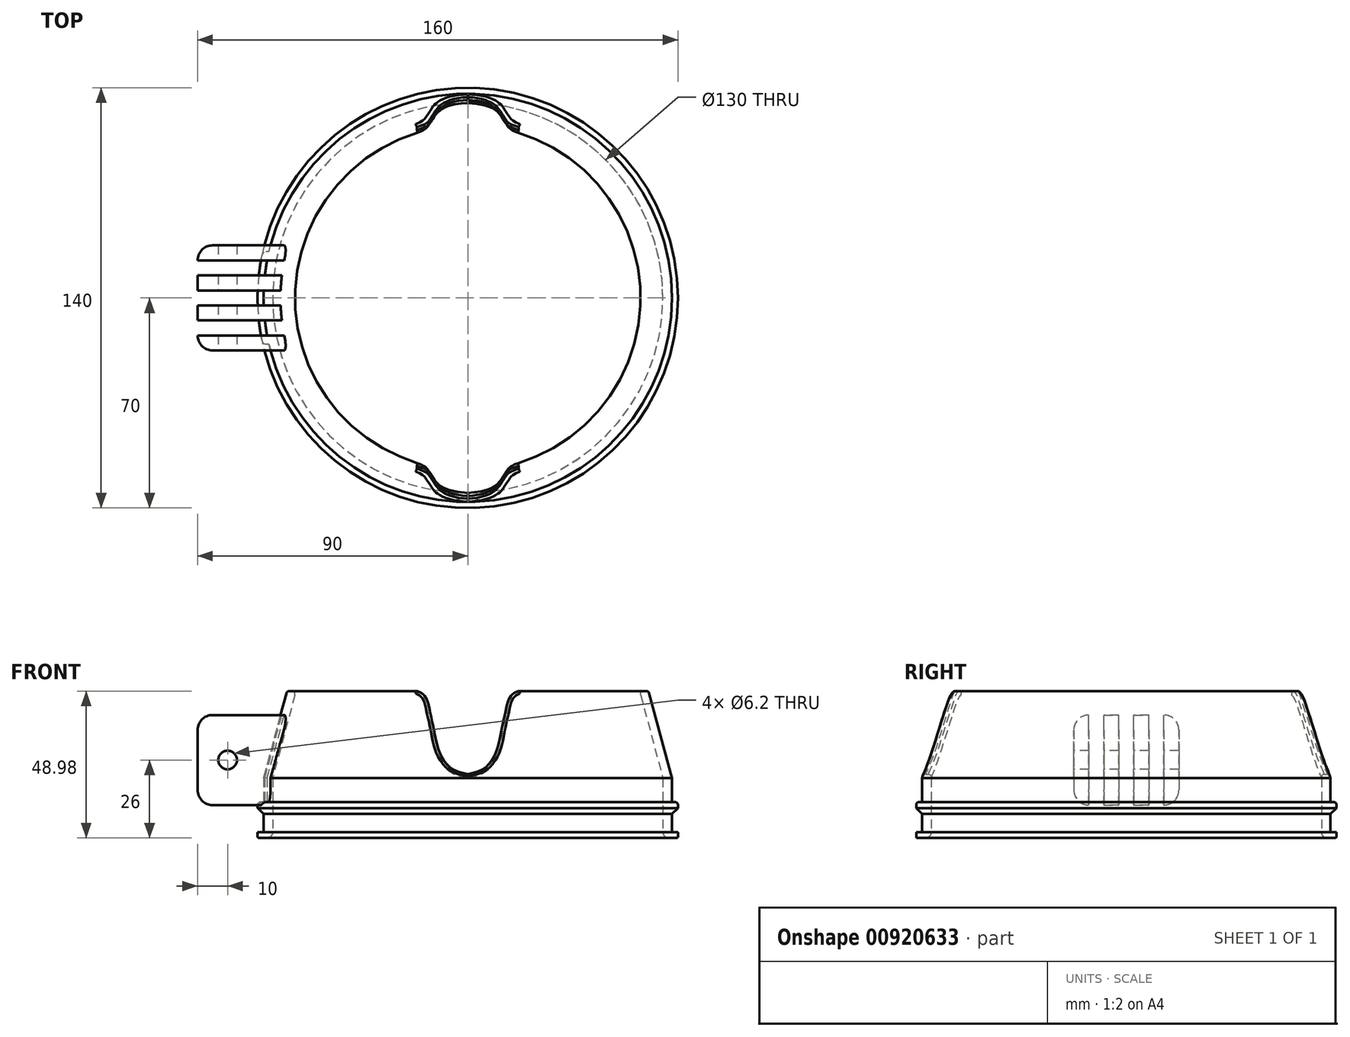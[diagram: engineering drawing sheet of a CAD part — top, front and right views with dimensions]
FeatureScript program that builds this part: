
annotation { "Feature Type Name" : "Feature", "Feature Type Description" : "" }
export const myFeature = defineFeature(function(context is Context, id is Id, definition is map)
    precondition{}
    {
        {
            var Q0;
            Q0=qCreatedBy(makeId("Front.planeOp"),FACE);
            var sketch = newSketch(context, id + "F0", { "sketchPlane" : qUnion([Q0])});
            skLineSegment(sketch, "E0.top", {"start": v(-68, 20) * mm, "end": v(-65, 20) * mm});
            skLineSegment(sketch, "E0.left", {"start": v(-68, 0) * mm, "end": v(-68, 20) * mm});
            skLineSegment(sketch, "E0.right", {"start": v(-65, 0) * mm, "end": v(-65, 20) * mm});
            skLineSegment(sketch, "E1", {"start": v(-68, 20) * mm, "end": v(-60.24, 48.98) * mm});
            skLineSegment(sketch, "E2", {"start": v(-57.24, 48.98) * mm, "end": v(-65, 20) * mm});
            skPoint(sketch, "E3.visualSharp", {"position": v(-68, 0) * mm});
            skPoint(sketch, "E4.visualSharp", {"position": v(-65, 0) * mm});
            skLineSegment(sketch, "E5", {"start": v(-68, 12) * mm, "end": v(-69, 12) * mm});
            skLineSegment(sketch, "E6", {"start": v(-70, 11) * mm, "end": v(-70, 10) * mm});
            skLineSegment(sketch, "E7", {"start": v(-70, 10) * mm, "end": v(-68, 8) * mm});
            skLineSegment(sketch, "E8", {"start": v(-68, 2) * mm, "end": v(-70, 2) * mm});
            skLineSegment(sketch, "E9", {"start": v(-70, 2) * mm, "end": v(-70, 0) * mm});
            skLineSegment(sketch, "E10", {"start": v(-70, 0) * mm, "end": v(-68, 0) * mm});
            skPoint(sketch, "E11.visualSharp", {"position": v(-70, 12) * mm});
            skArc(sketch, "E11.filletArc", {"start": v(-69, 12) * mm, "mid": v(-69.7, 11.7) * mm, "end": v(-70, 11) * mm});
            skLineSegment(sketch, "E12", {"start": v(0, 0) * mm, "end": v(0, 37.2) * mm, "construction": true});
            skLineSegment(sketch, "E13", {"start": v(-60.24, 48.98) * mm, "end": v(-57.24, 48.98) * mm});
            skLineSegment(sketch, "E14", {"start": v(-68, 0) * mm, "end": v(-65, 0) * mm});
            skSolve(sketch);
        }
        {
            var Q0;
            Q0=makeQuery(id+"F0.imprint","IMPRINT",FACE,{"disambiguationData":[TD([[makeQuery(id+"F0.imprint","IMPRINT",EDGE,{"derivedFrom":sQuery(id+"F0.wireOp",EDGE,"E0.bottom")}),1.0]])]});
            var Q1;
            {var subQ0=sQuery(id+"F0.wireOp",EDGE,"E0.top");Q1=makeQuery(id+"F0.imprint","IMPRINT",FACE,{"disambiguationData":[TD([[makeQuery(id+"F0.imprint","IMPRINT",EDGE,{"derivedFrom":subQ0}),1.0]])]});}
            var Q2;
            Q2=makeQuery(id+"F0.imprint","IMPRINT",FACE,{"disambiguationData":[TD([[makeQuery(id+"F0.imprint","IMPRINT",EDGE,{"derivedFrom":sQuery(id+"F0.wireOp",EDGE,"ip61VsO4-G4QX-MuCQ-3TD0-dqhbcXr0CBei")}),1.0]])]});
            var Q3;
            {var subQ1=sQuery(id+"F0.wireOp",EDGE,"E5");Q3=makeQuery(id+"F0.imprint","IMPRINT",FACE,{"disambiguationData":[TD([[makeQuery(id+"F0.imprint","IMPRINT",EDGE,{"derivedFrom":subQ1}),1.0]])]});}
            var Q4;
            {var subQ0=sQuery(id+"F0.wireOp",EDGE,"E8");Q4=makeQuery(id+"F0.imprint","IMPRINT",FACE,{"disambiguationData":[TD([[makeQuery(id+"F0.imprint","IMPRINT",EDGE,{"derivedFrom":subQ0}),1.0]])]});}
            var Q5;
            {var subQ5=sQuery(id+"F0.wireOp",EDGE,"E0.top");Q5=makeQuery(id+"F0.imprint","IMPRINT",FACE,{"disambiguationData":[TD([[makeQuery(id+"F0.imprint","IMPRINT",EDGE,{"derivedFrom":subQ5}),-1.0]])]});}
            var Q6;
            Q6=sQuery(id+"F0.wireOp",EDGE,"E12");
            revolve(context, id + "F1", {"surfaceOperationType" : NewSurfaceOperationType.NEW, "entities" : qUnion([Q0, Q1, Q2, Q3, Q4, Q5]), "axis" : qUnion([Q6]), "revolveType" : RevolveType.FULL});
        }
        {
            var Q0;
            Q0=qCreatedBy(makeId("Front.planeOp"),FACE);
            var sketch = newSketch(context, id + "F2", { "sketchPlane" : qUnion([Q0])});
            skFitSpline(sketch, "E15", {"points": [v(21.47, 49.66) * mm, v(17.18, 49.05) * mm, v(14.22, 47.2) * mm, v(12.69, 42.71) * mm, v(11.26, 35.97) * mm, v(9.52, 28.93) * mm, v(5.64, 23.3) * mm, v(0, 21.26) * mm], "startDerivative": vector(-35.25, -2.77) * mm, "endDerivative": vector(-40.6, -8.65) * mm});
            skFitSpline(sketch, "E16.MirrorCS", {"points": [v(-21.47, 49.66) * mm, v(-17.18, 49.05) * mm, v(-14.22, 47.2) * mm, v(-12.69, 42.71) * mm, v(-11.26, 35.97) * mm, v(-9.52, 28.93) * mm, v(-5.64, 23.3) * mm, v(0, 21.26) * mm], "startDerivative": vector(35.25, -2.77) * mm, "endDerivative": vector(40.6, -8.65) * mm});
            skLineSegment(sketch, "E17", {"start": v(21.47, 49.66) * mm, "end": v(21.47, 54.46) * mm});
            skLineSegment(sketch, "E18", {"start": v(21.47, 54.46) * mm, "end": v(-21.12, 54.46) * mm});
            skLineSegment(sketch, "E19", {"start": v(-21.12, 54.46) * mm, "end": v(-21.47, 49.66) * mm});
            skSolve(sketch);
        }
        {
            var Q0;
            Q0=qSketchRegion(id+"F2",true);
            extrude(context, id + "F3", {"entities" : qUnion([Q0]), "operationType" : NewBodyOperationType.REMOVE, "endBound" : BoundingType.SYMMETRIC, "depth" : 200 * mm, "offsetDistance" : 25 * mm});
        }
        {
            var Q0;
            Q0=qCreatedBy(makeId("Right.planeOp"),FACE);
            cPlane(context, id + "F4", {"entities" : qUnion([Q0]), "cplaneType" : CPlaneType.OFFSET, "offset" : 90 * mm, "oppositeDirection" : true, "width" : 150 * mm, "height" : 150 * mm});
        }
        {
            var Q0;
            Q0 = qSketchRegion(id + "F0", true);
            var Q1;
            Q1=sQuery(id+"F0.wireOp",EDGE,"E12");
            revolve(context, id + "F5", {"operationType" : NewBodyOperationType.ADD, "surfaceOperationType" : NewSurfaceOperationType.NEW, "entities" : qUnion([Q0]), "axis" : qUnion([Q1]), "revolveType" : RevolveType.SYMMETRIC, "angle" : 35 * degree});
        }
        {
            var Q0;
            Q0=qCreatedBy(id+"F4.planeOp",FACE);
            var sketch = newSketch(context, id + "F6", { "sketchPlane" : qUnion([Q0])});
            skLineSegment(sketch, "E20.bottom", {"start": v(-17.5, 41) * mm, "end": v(-12.5, 41) * mm});
            skLineSegment(sketch, "E20.left", {"start": v(-17.5, 41) * mm, "end": v(-17.5, 11) * mm});
            skLineSegment(sketch, "E20.right", {"start": v(-12.5, 41) * mm, "end": v(-12.5, 11) * mm});
            skLineSegment(sketch, "E21", {"start": v(-17.5, 11) * mm, "end": v(-12.5, 11) * mm});
            skLineSegment(sketch, "E22.1.0.0", {"start": v(-2.5, 41) * mm, "end": v(-2.5, 11) * mm});
            skLineSegment(sketch, "E22.1.0.1", {"start": v(-7.5, 41) * mm, "end": v(-7.5, 11) * mm});
            skLineSegment(sketch, "E22.1.0.2", {"start": v(-7.5, 41) * mm, "end": v(-2.5, 41) * mm});
            skLineSegment(sketch, "E22.1.0.3", {"start": v(-7.5, 11) * mm, "end": v(-2.5, 11) * mm});
            skLineSegment(sketch, "E22.2.0.0", {"start": v(7.5, 41) * mm, "end": v(7.5, 11) * mm});
            skLineSegment(sketch, "E22.2.0.1", {"start": v(2.5, 41) * mm, "end": v(2.5, 11) * mm});
            skLineSegment(sketch, "E22.2.0.2", {"start": v(2.5, 41) * mm, "end": v(7.5, 41) * mm});
            skLineSegment(sketch, "E22.2.0.3", {"start": v(2.5, 11) * mm, "end": v(7.5, 11) * mm});
            skLineSegment(sketch, "E22.3.0.0", {"start": v(17.5, 41) * mm, "end": v(17.5, 11) * mm});
            skLineSegment(sketch, "E22.3.0.1", {"start": v(12.5, 41) * mm, "end": v(12.5, 11) * mm});
            skLineSegment(sketch, "E22.3.0.2", {"start": v(12.5, 41) * mm, "end": v(17.5, 41) * mm});
            skLineSegment(sketch, "E22.3.0.3", {"start": v(12.5, 11) * mm, "end": v(17.5, 11) * mm});
            skLineSegment(sketch, "E22.direction1", {"start": v(-18.79, 11) * mm, "end": v(-8.79, 11) * mm, "construction": true});
            skSolve(sketch);
        }
        {
            var Q0;
            Q0=qSketchRegion(id+"F6",true);
            extrude(context, id + "F7", {"entities" : qUnion([Q0]), "operationType" : NewBodyOperationType.ADD, "endBound" : BoundingType.UP_TO_NEXT, "depth" : 25 * mm, "offsetDistance" : 25 * mm});
        }
        {
            var Q0;
            {var subQ0=sQuery(id+"F0.wireOp",EDGE,"E2");var subQ2=sQuery(id+"F0.wireOp",EDGE,"E13");var subQ4=makeQuery(id+"F3.opExtrude","SWEPT_FACE",FACE,{"disambiguationData":[OSD([sQuery(id+"F2.wireOp",EDGE,"E16.MirrorCS")])]});Q0=makeQuery(id+"Fq1PH19bnDTYdRj_1.1.F3.boolean.opBoolean","SPLIT",EDGE,{"disambiguationData":[TD([makeQuery(id+"F3.boolean.opBoolean","COPY",FACE,{"disambiguationData":[OD(0.0)],"derivedFrom":subQ4})])],"derivedFrom":makeQuery(id+"F3.boolean.opBoolean","SPLIT",EDGE,{"disambiguationData":[TD([subQ4])],"derivedFrom":makeQuery(id+"F1.opRevolve","SWEPT_EDGE",EDGE,{"disambiguationData":[OSD([subQ0,subQ2])]})})});}
            var Q1;
            Q1=makeQuery(id+"F3.boolean.opBoolean","INTERSECT",EDGE,{"disambiguationData":[OD(0.0)],"derivedFrom":[makeQuery(id+"F1.opRevolve","SWEPT_FACE",FACE,{"disambiguationData":[OSD([sQuery(id+"F0.wireOp",EDGE,"E2")])]}),makeQuery(id+"F3.opExtrude","SWEPT_FACE",FACE,{"disambiguationData":[OSD([sQuery(id+"F2.wireOp",EDGE,"E16.MirrorCS")])]})]});
            var Q2;
            Q2=makeQuery(id+"F3.boolean.opBoolean","INTERSECT",EDGE,{"disambiguationData":[OD(0.0)],"derivedFrom":[makeQuery(id+"F1.opRevolve","SWEPT_FACE",FACE,{"disambiguationData":[OSD([sQuery(id+"F0.wireOp",EDGE,"E2")])]}),makeQuery(id+"F3.opExtrude","SWEPT_FACE",FACE,{"disambiguationData":[OSD([sQuery(id+"F2.wireOp",EDGE,"E15")])]})]});
            var Q3;
            {var subQ0=sQuery(id+"F0.wireOp",EDGE,"E2");var subQ2=sQuery(id+"F2.wireOp",EDGE,"E15");var subQ3=makeQuery(id+"F3.opExtrude","SWEPT_FACE",FACE,{"disambiguationData":[OSD([subQ2])]});var subQ4=makeQuery(id+"F3.boolean.opBoolean","COPY",FACE,{"disambiguationData":[OD(0.0)],"derivedFrom":subQ3});var subQ5=sQuery(id+"F0.wireOp",EDGE,"E13");Q3=makeQuery(id+"Fq1PH19bnDTYdRj_1.3.F3.boolean.opBoolean","SPLIT",EDGE,{"disambiguationData":[TD([subQ4])],"derivedFrom":makeQuery(id+"Fq1PH19bnDTYdRj_1.2.F3.boolean.opBoolean","SPLIT",EDGE,{"disambiguationData":[TD([subQ4])],"derivedFrom":makeQuery(id+"Fq1PH19bnDTYdRj_1.1.F3.boolean.opBoolean","SPLIT",EDGE,{"disambiguationData":[TD([subQ4])],"derivedFrom":makeQuery(id+"F3.boolean.opBoolean","SPLIT",EDGE,{"disambiguationData":[TD([subQ3])],"derivedFrom":makeQuery(id+"F1.opRevolve","SWEPT_EDGE",EDGE,{"disambiguationData":[OSD([subQ0,subQ5])]})})})})});}
            var Q4;
            Q4=makeQuery(id+"Fq1PH19bnDTYdRj_1.3.F3.boolean.opBoolean","INTERSECT",EDGE,{"disambiguationData":[OD(1.0)],"derivedFrom":[makeQuery(id+"F1.opRevolve","SWEPT_FACE",FACE,{"disambiguationData":[OSD([sQuery(id+"F0.wireOp",EDGE,"E2")])]}),makeQuery(id+"Fq1PH19bnDTYdRj_1.3.F3.opExtrude","SWEPT_FACE",FACE,{"disambiguationData":[OSD([sQuery(id+"F2.wireOp",EDGE,"E15")])]})]});
            var Q5;
            Q5=makeQuery(id+"Fq1PH19bnDTYdRj_1.3.F3.boolean.opBoolean","INTERSECT",EDGE,{"disambiguationData":[OD(1.0)],"derivedFrom":[makeQuery(id+"F1.opRevolve","SWEPT_FACE",FACE,{"disambiguationData":[OSD([sQuery(id+"F0.wireOp",EDGE,"E2")])]}),makeQuery(id+"Fq1PH19bnDTYdRj_1.3.F3.opExtrude","SWEPT_FACE",FACE,{"disambiguationData":[OSD([sQuery(id+"F2.wireOp",EDGE,"E16.MirrorCS")])]})]});
            var Q6;
            {var subQ0=sQuery(id+"F0.wireOp",EDGE,"E2");var subQ2=sQuery(id+"F0.wireOp",EDGE,"E13");var subQ4=sQuery(id+"F2.wireOp",EDGE,"E15");var subQ5=makeQuery(id+"Fq1PH19bnDTYdRj_1.2.F3.opExtrude","SWEPT_FACE",FACE,{"disambiguationData":[OSD([subQ4])]});var subQ6=makeQuery(id+"F3.opExtrude","SWEPT_FACE",FACE,{"disambiguationData":[OSD([subQ4])]});var subQ7=makeQuery(id+"F3.boolean.opBoolean","COPY",FACE,{"disambiguationData":[OD(0.0)],"derivedFrom":subQ6});Q6=makeQuery(id+"Fq1PH19bnDTYdRj_1.3.F3.boolean.opBoolean","SPLIT",EDGE,{"disambiguationData":[TD([makeQuery(id+"Fq1PH19bnDTYdRj_1.2.F3.boolean.opBoolean","COPY",FACE,{"disambiguationData":[OD(1.0)],"derivedFrom":subQ5})])],"derivedFrom":makeQuery(id+"Fq1PH19bnDTYdRj_1.2.F3.boolean.opBoolean","SPLIT",EDGE,{"disambiguationData":[TD([subQ7])],"derivedFrom":makeQuery(id+"Fq1PH19bnDTYdRj_1.1.F3.boolean.opBoolean","SPLIT",EDGE,{"disambiguationData":[TD([subQ7])],"derivedFrom":makeQuery(id+"F3.boolean.opBoolean","SPLIT",EDGE,{"disambiguationData":[TD([subQ6])],"derivedFrom":makeQuery(id+"F1.opRevolve","SWEPT_EDGE",EDGE,{"disambiguationData":[OSD([subQ0,subQ2])]})})})})});}
            var Q7;
            Q7=makeQuery(id+"Fq1PH19bnDTYdRj_1.2.F3.boolean.opBoolean","INTERSECT",EDGE,{"disambiguationData":[OD(1.0)],"derivedFrom":[makeQuery(id+"F1.opRevolve","SWEPT_FACE",FACE,{"disambiguationData":[OSD([sQuery(id+"F0.wireOp",EDGE,"E2")])]}),makeQuery(id+"Fq1PH19bnDTYdRj_1.2.F3.opExtrude","SWEPT_FACE",FACE,{"disambiguationData":[OSD([sQuery(id+"F2.wireOp",EDGE,"E15")])]})]});
            var Q8;
            Q8=makeQuery(id+"Fq1PH19bnDTYdRj_1.2.F3.boolean.opBoolean","INTERSECT",EDGE,{"disambiguationData":[OD(1.0)],"derivedFrom":[makeQuery(id+"F1.opRevolve","SWEPT_FACE",FACE,{"disambiguationData":[OSD([sQuery(id+"F0.wireOp",EDGE,"E2")])]}),makeQuery(id+"Fq1PH19bnDTYdRj_1.2.F3.opExtrude","SWEPT_FACE",FACE,{"disambiguationData":[OSD([sQuery(id+"F2.wireOp",EDGE,"E16.MirrorCS")])]})]});
            var Q9;
            {var subQ0=sQuery(id+"F0.wireOp",EDGE,"E2");var subQ2=sQuery(id+"F2.wireOp",EDGE,"E15");var subQ3=makeQuery(id+"Fq1PH19bnDTYdRj_1.1.F3.opExtrude","SWEPT_FACE",FACE,{"disambiguationData":[OSD([subQ2])]});var subQ4=sQuery(id+"F0.wireOp",EDGE,"E13");var subQ6=makeQuery(id+"F3.opExtrude","SWEPT_FACE",FACE,{"disambiguationData":[OSD([subQ2])]});Q9=makeQuery(id+"Fq1PH19bnDTYdRj_1.2.F3.boolean.opBoolean","SPLIT",EDGE,{"disambiguationData":[TD([makeQuery(id+"Fq1PH19bnDTYdRj_1.1.F3.boolean.opBoolean","COPY",FACE,{"disambiguationData":[OD(1.0)],"derivedFrom":subQ3})])],"derivedFrom":makeQuery(id+"Fq1PH19bnDTYdRj_1.1.F3.boolean.opBoolean","SPLIT",EDGE,{"disambiguationData":[TD([makeQuery(id+"F3.boolean.opBoolean","COPY",FACE,{"disambiguationData":[OD(0.0)],"derivedFrom":subQ6})])],"derivedFrom":makeQuery(id+"F3.boolean.opBoolean","SPLIT",EDGE,{"disambiguationData":[TD([subQ6])],"derivedFrom":makeQuery(id+"F1.opRevolve","SWEPT_EDGE",EDGE,{"disambiguationData":[OSD([subQ0,subQ4])]})})})});}
            var Q10;
            Q10=makeQuery(id+"Fq1PH19bnDTYdRj_1.1.F3.boolean.opBoolean","INTERSECT",EDGE,{"disambiguationData":[OD(1.0)],"derivedFrom":[makeQuery(id+"F1.opRevolve","SWEPT_FACE",FACE,{"disambiguationData":[OSD([sQuery(id+"F0.wireOp",EDGE,"E2")])]}),makeQuery(id+"Fq1PH19bnDTYdRj_1.1.F3.opExtrude","SWEPT_FACE",FACE,{"disambiguationData":[OSD([sQuery(id+"F2.wireOp",EDGE,"E15")])]})]});
            var Q11;
            Q11=makeQuery(id+"Fq1PH19bnDTYdRj_1.1.F3.boolean.opBoolean","INTERSECT",EDGE,{"disambiguationData":[OD(1.0)],"derivedFrom":[makeQuery(id+"F1.opRevolve","SWEPT_FACE",FACE,{"disambiguationData":[OSD([sQuery(id+"F0.wireOp",EDGE,"E2")])]}),makeQuery(id+"Fq1PH19bnDTYdRj_1.1.F3.opExtrude","SWEPT_FACE",FACE,{"disambiguationData":[OSD([sQuery(id+"F2.wireOp",EDGE,"E16.MirrorCS")])]})]});
            var Q12;
            {var subQ0=sQuery(id+"F0.wireOp",EDGE,"E2");var subQ2=sQuery(id+"F0.wireOp",EDGE,"E13");var subQ4=makeQuery(id+"F3.opExtrude","SWEPT_FACE",FACE,{"disambiguationData":[OSD([sQuery(id+"F2.wireOp",EDGE,"E15")])]});Q12=makeQuery(id+"Fq1PH19bnDTYdRj_1.1.F3.boolean.opBoolean","SPLIT",EDGE,{"disambiguationData":[TD([makeQuery(id+"F3.boolean.opBoolean","COPY",FACE,{"disambiguationData":[OD(1.0)],"derivedFrom":subQ4})])],"derivedFrom":makeQuery(id+"F3.boolean.opBoolean","SPLIT",EDGE,{"disambiguationData":[TD([subQ4])],"derivedFrom":makeQuery(id+"F1.opRevolve","SWEPT_EDGE",EDGE,{"disambiguationData":[OSD([subQ0,subQ2])]})})});}
            var Q13;
            Q13=makeQuery(id+"F3.boolean.opBoolean","INTERSECT",EDGE,{"disambiguationData":[OD(1.0)],"derivedFrom":[makeQuery(id+"F1.opRevolve","SWEPT_FACE",FACE,{"disambiguationData":[OSD([sQuery(id+"F0.wireOp",EDGE,"E2")])]}),makeQuery(id+"F3.opExtrude","SWEPT_FACE",FACE,{"disambiguationData":[OSD([sQuery(id+"F2.wireOp",EDGE,"E15")])]})]});
            var Q14;
            Q14=makeQuery(id+"F3.boolean.opBoolean","INTERSECT",EDGE,{"disambiguationData":[OD(1.0)],"derivedFrom":[makeQuery(id+"F1.opRevolve","SWEPT_FACE",FACE,{"disambiguationData":[OSD([sQuery(id+"F0.wireOp",EDGE,"E2")])]}),makeQuery(id+"F3.opExtrude","SWEPT_FACE",FACE,{"disambiguationData":[OSD([sQuery(id+"F2.wireOp",EDGE,"E16.MirrorCS")])]})]});
            var Q15;
            {var subQ0=sQuery(id+"F0.wireOp",EDGE,"E2");var subQ2=sQuery(id+"F0.wireOp",EDGE,"E13");var subQ4=sQuery(id+"F2.wireOp",EDGE,"E16.MirrorCS");var subQ5=makeQuery(id+"F3.opExtrude","SWEPT_FACE",FACE,{"disambiguationData":[OSD([subQ4])]});var subQ6=makeQuery(id+"F3.boolean.opBoolean","COPY",FACE,{"disambiguationData":[OD(1.0)],"derivedFrom":subQ5});Q15=makeQuery(id+"Fq1PH19bnDTYdRj_1.3.F3.boolean.opBoolean","SPLIT",EDGE,{"disambiguationData":[TD([subQ6])],"derivedFrom":makeQuery(id+"Fq1PH19bnDTYdRj_1.2.F3.boolean.opBoolean","SPLIT",EDGE,{"disambiguationData":[TD([subQ6])],"derivedFrom":makeQuery(id+"Fq1PH19bnDTYdRj_1.1.F3.boolean.opBoolean","SPLIT",EDGE,{"disambiguationData":[TD([subQ6])],"derivedFrom":makeQuery(id+"F3.boolean.opBoolean","SPLIT",EDGE,{"disambiguationData":[TD([subQ5])],"derivedFrom":makeQuery(id+"F1.opRevolve","SWEPT_EDGE",EDGE,{"disambiguationData":[OSD([subQ0,subQ2])]})})})})});}
            var Q16;
            Q16=makeQuery(id+"Fq1PH19bnDTYdRj_1.3.F3.boolean.opBoolean","INTERSECT",EDGE,{"disambiguationData":[OD(0.0)],"derivedFrom":[makeQuery(id+"F1.opRevolve","SWEPT_FACE",FACE,{"disambiguationData":[OSD([sQuery(id+"F0.wireOp",EDGE,"E2")])]}),makeQuery(id+"Fq1PH19bnDTYdRj_1.3.F3.opExtrude","SWEPT_FACE",FACE,{"disambiguationData":[OSD([sQuery(id+"F2.wireOp",EDGE,"E16.MirrorCS")])]})]});
            var Q17;
            Q17=makeQuery(id+"Fq1PH19bnDTYdRj_1.3.F3.boolean.opBoolean","INTERSECT",EDGE,{"disambiguationData":[OD(0.0)],"derivedFrom":[makeQuery(id+"F1.opRevolve","SWEPT_FACE",FACE,{"disambiguationData":[OSD([sQuery(id+"F0.wireOp",EDGE,"E2")])]}),makeQuery(id+"Fq1PH19bnDTYdRj_1.3.F3.opExtrude","SWEPT_FACE",FACE,{"disambiguationData":[OSD([sQuery(id+"F2.wireOp",EDGE,"E15")])]})]});
            var Q18;
            {var subQ0=sQuery(id+"F0.wireOp",EDGE,"E2");var subQ2=sQuery(id+"F0.wireOp",EDGE,"E13");var subQ4=sQuery(id+"F2.wireOp",EDGE,"E16.MirrorCS");var subQ5=makeQuery(id+"Fq1PH19bnDTYdRj_1.2.F3.opExtrude","SWEPT_FACE",FACE,{"disambiguationData":[OSD([subQ4])]});var subQ6=makeQuery(id+"F3.opExtrude","SWEPT_FACE",FACE,{"disambiguationData":[OSD([subQ4])]});var subQ7=makeQuery(id+"F3.boolean.opBoolean","COPY",FACE,{"disambiguationData":[OD(1.0)],"derivedFrom":subQ6});Q18=makeQuery(id+"Fq1PH19bnDTYdRj_1.3.F3.boolean.opBoolean","SPLIT",EDGE,{"disambiguationData":[TD([makeQuery(id+"Fq1PH19bnDTYdRj_1.2.F3.boolean.opBoolean","COPY",FACE,{"disambiguationData":[OD(0.0)],"derivedFrom":subQ5})])],"derivedFrom":makeQuery(id+"Fq1PH19bnDTYdRj_1.2.F3.boolean.opBoolean","SPLIT",EDGE,{"disambiguationData":[TD([subQ7])],"derivedFrom":makeQuery(id+"Fq1PH19bnDTYdRj_1.1.F3.boolean.opBoolean","SPLIT",EDGE,{"disambiguationData":[TD([subQ7])],"derivedFrom":makeQuery(id+"F3.boolean.opBoolean","SPLIT",EDGE,{"disambiguationData":[TD([subQ6])],"derivedFrom":makeQuery(id+"F1.opRevolve","SWEPT_EDGE",EDGE,{"disambiguationData":[OSD([subQ0,subQ2])]})})})})});}
            var Q19;
            Q19=makeQuery(id+"Fq1PH19bnDTYdRj_1.2.F3.boolean.opBoolean","INTERSECT",EDGE,{"disambiguationData":[OD(0.0)],"derivedFrom":[makeQuery(id+"F1.opRevolve","SWEPT_FACE",FACE,{"disambiguationData":[OSD([sQuery(id+"F0.wireOp",EDGE,"E2")])]}),makeQuery(id+"Fq1PH19bnDTYdRj_1.2.F3.opExtrude","SWEPT_FACE",FACE,{"disambiguationData":[OSD([sQuery(id+"F2.wireOp",EDGE,"E16.MirrorCS")])]})]});
            var Q20;
            Q20=makeQuery(id+"Fq1PH19bnDTYdRj_1.2.F3.boolean.opBoolean","INTERSECT",EDGE,{"disambiguationData":[OD(0.0)],"derivedFrom":[makeQuery(id+"F1.opRevolve","SWEPT_FACE",FACE,{"disambiguationData":[OSD([sQuery(id+"F0.wireOp",EDGE,"E2")])]}),makeQuery(id+"Fq1PH19bnDTYdRj_1.2.F3.opExtrude","SWEPT_FACE",FACE,{"disambiguationData":[OSD([sQuery(id+"F2.wireOp",EDGE,"E15")])]})]});
            var Q21;
            {var subQ0=sQuery(id+"F0.wireOp",EDGE,"E2");var subQ2=sQuery(id+"F0.wireOp",EDGE,"E13");var subQ4=sQuery(id+"F2.wireOp",EDGE,"E16.MirrorCS");var subQ5=makeQuery(id+"Fq1PH19bnDTYdRj_1.1.F3.opExtrude","SWEPT_FACE",FACE,{"disambiguationData":[OSD([subQ4])]});var subQ6=makeQuery(id+"F3.opExtrude","SWEPT_FACE",FACE,{"disambiguationData":[OSD([subQ4])]});Q21=makeQuery(id+"Fq1PH19bnDTYdRj_1.2.F3.boolean.opBoolean","SPLIT",EDGE,{"disambiguationData":[TD([makeQuery(id+"Fq1PH19bnDTYdRj_1.1.F3.boolean.opBoolean","COPY",FACE,{"disambiguationData":[OD(0.0)],"derivedFrom":subQ5})])],"derivedFrom":makeQuery(id+"Fq1PH19bnDTYdRj_1.1.F3.boolean.opBoolean","SPLIT",EDGE,{"disambiguationData":[TD([makeQuery(id+"F3.boolean.opBoolean","COPY",FACE,{"disambiguationData":[OD(1.0)],"derivedFrom":subQ6})])],"derivedFrom":makeQuery(id+"F3.boolean.opBoolean","SPLIT",EDGE,{"disambiguationData":[TD([subQ6])],"derivedFrom":makeQuery(id+"F1.opRevolve","SWEPT_EDGE",EDGE,{"disambiguationData":[OSD([subQ0,subQ2])]})})})});}
            var Q22;
            Q22=makeQuery(id+"Fq1PH19bnDTYdRj_1.1.F3.boolean.opBoolean","INTERSECT",EDGE,{"disambiguationData":[OD(0.0)],"derivedFrom":[makeQuery(id+"F1.opRevolve","SWEPT_FACE",FACE,{"disambiguationData":[OSD([sQuery(id+"F0.wireOp",EDGE,"E2")])]}),makeQuery(id+"Fq1PH19bnDTYdRj_1.1.F3.opExtrude","SWEPT_FACE",FACE,{"disambiguationData":[OSD([sQuery(id+"F2.wireOp",EDGE,"E16.MirrorCS")])]})]});
            var Q23;
            Q23=makeQuery(id+"Fq1PH19bnDTYdRj_1.1.F3.boolean.opBoolean","INTERSECT",EDGE,{"disambiguationData":[OD(0.0)],"derivedFrom":[makeQuery(id+"F1.opRevolve","SWEPT_FACE",FACE,{"disambiguationData":[OSD([sQuery(id+"F0.wireOp",EDGE,"E2")])]}),makeQuery(id+"Fq1PH19bnDTYdRj_1.1.F3.opExtrude","SWEPT_FACE",FACE,{"disambiguationData":[OSD([sQuery(id+"F2.wireOp",EDGE,"E15")])]})]});
            fillet(context, id + "F8", {"entities" : qUnion([Q0, Q1, Q2, Q3, Q4, Q5, Q6, Q7, Q8, Q9, Q10, Q11, Q12, Q13, Q14, Q15, Q16, Q17, Q18, Q19, Q20, Q21, Q22, Q23]), "radius" : 1 * mm, "tangentPropagation" : true, "allowEdgeOverflow" : false});
        }
        {
            var Q0;
            {var subQ0=sQuery(id+"F0.wireOp",EDGE,"E1");var subQ2=sQuery(id+"F0.wireOp",EDGE,"E13");var subQ4=sQuery(id+"F2.wireOp",EDGE,"E15");var subQ5=makeQuery(id+"Fq1PH19bnDTYdRj_1.1.F3.opExtrude","SWEPT_FACE",FACE,{"disambiguationData":[OSD([subQ4])]});var subQ6=makeQuery(id+"F3.opExtrude","SWEPT_FACE",FACE,{"disambiguationData":[OSD([subQ4])]});Q0=makeQuery(id+"Fq1PH19bnDTYdRj_1.2.F3.boolean.opBoolean","SPLIT",EDGE,{"disambiguationData":[TD([makeQuery(id+"Fq1PH19bnDTYdRj_1.1.F3.boolean.opBoolean","COPY",FACE,{"disambiguationData":[OD(1.0)],"derivedFrom":subQ5})])],"derivedFrom":makeQuery(id+"Fq1PH19bnDTYdRj_1.1.F3.boolean.opBoolean","SPLIT",EDGE,{"disambiguationData":[TD([makeQuery(id+"F3.boolean.opBoolean","COPY",FACE,{"disambiguationData":[OD(0.0)],"derivedFrom":subQ6})])],"derivedFrom":makeQuery(id+"F3.boolean.opBoolean","SPLIT",EDGE,{"disambiguationData":[TD([subQ6])],"derivedFrom":makeQuery(id+"F1.opRevolve","SWEPT_EDGE",EDGE,{"disambiguationData":[OSD([subQ0,subQ2])]})})})});}
            var Q1;
            Q1=makeQuery(id+"Fq1PH19bnDTYdRj_1.2.F3.boolean.opBoolean","INTERSECT",EDGE,{"disambiguationData":[OD(1.0)],"derivedFrom":[makeQuery(id+"F1.opRevolve","SWEPT_FACE",FACE,{"disambiguationData":[OSD([sQuery(id+"F0.wireOp",EDGE,"E1")])]}),makeQuery(id+"Fq1PH19bnDTYdRj_1.2.F3.opExtrude","SWEPT_FACE",FACE,{"disambiguationData":[OSD([sQuery(id+"F2.wireOp",EDGE,"E16.MirrorCS")])]})]});
            var Q2;
            Q2=makeQuery(id+"Fq1PH19bnDTYdRj_1.2.F3.boolean.opBoolean","INTERSECT",EDGE,{"disambiguationData":[OD(1.0)],"derivedFrom":[makeQuery(id+"F1.opRevolve","SWEPT_FACE",FACE,{"disambiguationData":[OSD([sQuery(id+"F0.wireOp",EDGE,"E1")])]}),makeQuery(id+"Fq1PH19bnDTYdRj_1.2.F3.opExtrude","SWEPT_FACE",FACE,{"disambiguationData":[OSD([sQuery(id+"F2.wireOp",EDGE,"E15")])]})]});
            var Q3;
            Q3=makeQuery(id+"Fq1PH19bnDTYdRj_1.3.F3.boolean.opBoolean","INTERSECT",EDGE,{"disambiguationData":[OD(1.0)],"derivedFrom":[makeQuery(id+"F1.opRevolve","SWEPT_FACE",FACE,{"disambiguationData":[OSD([sQuery(id+"F0.wireOp",EDGE,"E1")])]}),makeQuery(id+"Fq1PH19bnDTYdRj_1.3.F3.opExtrude","SWEPT_FACE",FACE,{"disambiguationData":[OSD([sQuery(id+"F2.wireOp",EDGE,"E16.MirrorCS")])]})]});
            var Q4;
            {var subQ0=sQuery(id+"F0.wireOp",EDGE,"E1");var subQ2=sQuery(id+"F0.wireOp",EDGE,"E13");var subQ4=sQuery(id+"F2.wireOp",EDGE,"E15");var subQ5=makeQuery(id+"Fq1PH19bnDTYdRj_1.2.F3.opExtrude","SWEPT_FACE",FACE,{"disambiguationData":[OSD([subQ4])]});var subQ6=makeQuery(id+"F3.opExtrude","SWEPT_FACE",FACE,{"disambiguationData":[OSD([subQ4])]});var subQ7=makeQuery(id+"F3.boolean.opBoolean","COPY",FACE,{"disambiguationData":[OD(0.0)],"derivedFrom":subQ6});Q4=makeQuery(id+"Fq1PH19bnDTYdRj_1.3.F3.boolean.opBoolean","SPLIT",EDGE,{"disambiguationData":[TD([makeQuery(id+"Fq1PH19bnDTYdRj_1.2.F3.boolean.opBoolean","COPY",FACE,{"disambiguationData":[OD(1.0)],"derivedFrom":subQ5})])],"derivedFrom":makeQuery(id+"Fq1PH19bnDTYdRj_1.2.F3.boolean.opBoolean","SPLIT",EDGE,{"disambiguationData":[TD([subQ7])],"derivedFrom":makeQuery(id+"Fq1PH19bnDTYdRj_1.1.F3.boolean.opBoolean","SPLIT",EDGE,{"disambiguationData":[TD([subQ7])],"derivedFrom":makeQuery(id+"F3.boolean.opBoolean","SPLIT",EDGE,{"disambiguationData":[TD([subQ6])],"derivedFrom":makeQuery(id+"F1.opRevolve","SWEPT_EDGE",EDGE,{"disambiguationData":[OSD([subQ0,subQ2])]})})})})});}
            var Q5;
            Q5=makeQuery(id+"Fq1PH19bnDTYdRj_1.3.F3.boolean.opBoolean","INTERSECT",EDGE,{"disambiguationData":[OD(1.0)],"derivedFrom":[makeQuery(id+"F1.opRevolve","SWEPT_FACE",FACE,{"disambiguationData":[OSD([sQuery(id+"F0.wireOp",EDGE,"E1")])]}),makeQuery(id+"Fq1PH19bnDTYdRj_1.3.F3.opExtrude","SWEPT_FACE",FACE,{"disambiguationData":[OSD([sQuery(id+"F2.wireOp",EDGE,"E15")])]})]});
            var Q6;
            Q6=makeQuery(id+"F3.boolean.opBoolean","INTERSECT",EDGE,{"disambiguationData":[OD(0.0)],"derivedFrom":[makeQuery(id+"F1.opRevolve","SWEPT_FACE",FACE,{"disambiguationData":[OSD([sQuery(id+"F0.wireOp",EDGE,"E1")])]}),makeQuery(id+"F3.opExtrude","SWEPT_FACE",FACE,{"disambiguationData":[OSD([sQuery(id+"F2.wireOp",EDGE,"E15")])]})]});
            var Q7;
            {var subQ0=sQuery(id+"F0.wireOp",EDGE,"E1");var subQ2=sQuery(id+"F0.wireOp",EDGE,"E13");var subQ4=sQuery(id+"F2.wireOp",EDGE,"E15");var subQ5=makeQuery(id+"F3.opExtrude","SWEPT_FACE",FACE,{"disambiguationData":[OSD([subQ4])]});var subQ6=makeQuery(id+"F3.boolean.opBoolean","COPY",FACE,{"disambiguationData":[OD(0.0)],"derivedFrom":subQ5});Q7=makeQuery(id+"Fq1PH19bnDTYdRj_1.3.F3.boolean.opBoolean","SPLIT",EDGE,{"disambiguationData":[TD([subQ6])],"derivedFrom":makeQuery(id+"Fq1PH19bnDTYdRj_1.2.F3.boolean.opBoolean","SPLIT",EDGE,{"disambiguationData":[TD([subQ6])],"derivedFrom":makeQuery(id+"Fq1PH19bnDTYdRj_1.1.F3.boolean.opBoolean","SPLIT",EDGE,{"disambiguationData":[TD([subQ6])],"derivedFrom":makeQuery(id+"F3.boolean.opBoolean","SPLIT",EDGE,{"disambiguationData":[TD([subQ5])],"derivedFrom":makeQuery(id+"F1.opRevolve","SWEPT_EDGE",EDGE,{"disambiguationData":[OSD([subQ0,subQ2])]})})})})});}
            var Q8;
            Q8=makeQuery(id+"F3.boolean.opBoolean","INTERSECT",EDGE,{"disambiguationData":[OD(0.0)],"derivedFrom":[makeQuery(id+"F1.opRevolve","SWEPT_FACE",FACE,{"disambiguationData":[OSD([sQuery(id+"F0.wireOp",EDGE,"E1")])]}),makeQuery(id+"F3.opExtrude","SWEPT_FACE",FACE,{"disambiguationData":[OSD([sQuery(id+"F2.wireOp",EDGE,"E16.MirrorCS")])]})]});
            var Q9;
            Q9=makeQuery(id+"Fq1PH19bnDTYdRj_1.1.F3.boolean.opBoolean","INTERSECT",EDGE,{"disambiguationData":[OD(0.0)],"derivedFrom":[makeQuery(id+"F1.opRevolve","SWEPT_FACE",FACE,{"disambiguationData":[OSD([sQuery(id+"F0.wireOp",EDGE,"E1")])]}),makeQuery(id+"Fq1PH19bnDTYdRj_1.1.F3.opExtrude","SWEPT_FACE",FACE,{"disambiguationData":[OSD([sQuery(id+"F2.wireOp",EDGE,"E15")])]})]});
            var Q10;
            {var subQ0=sQuery(id+"F0.wireOp",EDGE,"E1");var subQ2=sQuery(id+"F0.wireOp",EDGE,"E13");var subQ4=makeQuery(id+"F3.opExtrude","SWEPT_FACE",FACE,{"disambiguationData":[OSD([sQuery(id+"F2.wireOp",EDGE,"E16.MirrorCS")])]});Q10=makeQuery(id+"Fq1PH19bnDTYdRj_1.1.F3.boolean.opBoolean","SPLIT",EDGE,{"disambiguationData":[TD([makeQuery(id+"F3.boolean.opBoolean","COPY",FACE,{"disambiguationData":[OD(0.0)],"derivedFrom":subQ4})])],"derivedFrom":makeQuery(id+"F3.boolean.opBoolean","SPLIT",EDGE,{"disambiguationData":[TD([subQ4])],"derivedFrom":makeQuery(id+"F1.opRevolve","SWEPT_EDGE",EDGE,{"disambiguationData":[OSD([subQ0,subQ2])]})})});}
            var Q11;
            Q11=makeQuery(id+"Fq1PH19bnDTYdRj_1.1.F3.boolean.opBoolean","INTERSECT",EDGE,{"disambiguationData":[OD(0.0)],"derivedFrom":[makeQuery(id+"F1.opRevolve","SWEPT_FACE",FACE,{"disambiguationData":[OSD([sQuery(id+"F0.wireOp",EDGE,"E1")])]}),makeQuery(id+"Fq1PH19bnDTYdRj_1.1.F3.opExtrude","SWEPT_FACE",FACE,{"disambiguationData":[OSD([sQuery(id+"F2.wireOp",EDGE,"E16.MirrorCS")])]})]});
            var Q12;
            Q12=makeQuery(id+"Fq1PH19bnDTYdRj_1.2.F3.boolean.opBoolean","INTERSECT",EDGE,{"disambiguationData":[OD(0.0)],"derivedFrom":[makeQuery(id+"F1.opRevolve","SWEPT_FACE",FACE,{"disambiguationData":[OSD([sQuery(id+"F0.wireOp",EDGE,"E1")])]}),makeQuery(id+"Fq1PH19bnDTYdRj_1.2.F3.opExtrude","SWEPT_FACE",FACE,{"disambiguationData":[OSD([sQuery(id+"F2.wireOp",EDGE,"E15")])]})]});
            var Q13;
            Q13=makeQuery(id+"Fq1PH19bnDTYdRj_1.2.F3.boolean.opBoolean","INTERSECT",EDGE,{"disambiguationData":[OD(0.0)],"derivedFrom":[makeQuery(id+"F1.opRevolve","SWEPT_FACE",FACE,{"disambiguationData":[OSD([sQuery(id+"F0.wireOp",EDGE,"E1")])]}),makeQuery(id+"Fq1PH19bnDTYdRj_1.2.F3.opExtrude","SWEPT_FACE",FACE,{"disambiguationData":[OSD([sQuery(id+"F2.wireOp",EDGE,"E16.MirrorCS")])]})]});
            var Q14;
            Q14=makeQuery(id+"Fq1PH19bnDTYdRj_1.3.F3.boolean.opBoolean","INTERSECT",EDGE,{"disambiguationData":[OD(0.0)],"derivedFrom":[makeQuery(id+"F1.opRevolve","SWEPT_FACE",FACE,{"disambiguationData":[OSD([sQuery(id+"F0.wireOp",EDGE,"E1")])]}),makeQuery(id+"Fq1PH19bnDTYdRj_1.3.F3.opExtrude","SWEPT_FACE",FACE,{"disambiguationData":[OSD([sQuery(id+"F2.wireOp",EDGE,"E15")])]})]});
            var Q15;
            {var subQ0=sQuery(id+"F0.wireOp",EDGE,"E1");var subQ2=sQuery(id+"F0.wireOp",EDGE,"E13");var subQ4=sQuery(id+"F2.wireOp",EDGE,"E16.MirrorCS");var subQ5=makeQuery(id+"Fq1PH19bnDTYdRj_1.2.F3.opExtrude","SWEPT_FACE",FACE,{"disambiguationData":[OSD([subQ4])]});var subQ6=makeQuery(id+"F3.opExtrude","SWEPT_FACE",FACE,{"disambiguationData":[OSD([subQ4])]});var subQ7=makeQuery(id+"F3.boolean.opBoolean","COPY",FACE,{"disambiguationData":[OD(1.0)],"derivedFrom":subQ6});Q15=makeQuery(id+"Fq1PH19bnDTYdRj_1.3.F3.boolean.opBoolean","SPLIT",EDGE,{"disambiguationData":[TD([makeQuery(id+"Fq1PH19bnDTYdRj_1.2.F3.boolean.opBoolean","COPY",FACE,{"disambiguationData":[OD(0.0)],"derivedFrom":subQ5})])],"derivedFrom":makeQuery(id+"Fq1PH19bnDTYdRj_1.2.F3.boolean.opBoolean","SPLIT",EDGE,{"disambiguationData":[TD([subQ7])],"derivedFrom":makeQuery(id+"Fq1PH19bnDTYdRj_1.1.F3.boolean.opBoolean","SPLIT",EDGE,{"disambiguationData":[TD([subQ7])],"derivedFrom":makeQuery(id+"F3.boolean.opBoolean","SPLIT",EDGE,{"disambiguationData":[TD([subQ6])],"derivedFrom":makeQuery(id+"F1.opRevolve","SWEPT_EDGE",EDGE,{"disambiguationData":[OSD([subQ0,subQ2])]})})})})});}
            var Q16;
            {var subQ0=sQuery(id+"F0.wireOp",EDGE,"E1");var subQ2=sQuery(id+"F0.wireOp",EDGE,"E13");var subQ4=sQuery(id+"F2.wireOp",EDGE,"E16.MirrorCS");var subQ5=makeQuery(id+"Fq1PH19bnDTYdRj_1.1.F3.opExtrude","SWEPT_FACE",FACE,{"disambiguationData":[OSD([subQ4])]});var subQ6=makeQuery(id+"F3.opExtrude","SWEPT_FACE",FACE,{"disambiguationData":[OSD([subQ4])]});Q16=makeQuery(id+"Fq1PH19bnDTYdRj_1.2.F3.boolean.opBoolean","SPLIT",EDGE,{"disambiguationData":[TD([makeQuery(id+"Fq1PH19bnDTYdRj_1.1.F3.boolean.opBoolean","COPY",FACE,{"disambiguationData":[OD(0.0)],"derivedFrom":subQ5})])],"derivedFrom":makeQuery(id+"Fq1PH19bnDTYdRj_1.1.F3.boolean.opBoolean","SPLIT",EDGE,{"disambiguationData":[TD([makeQuery(id+"F3.boolean.opBoolean","COPY",FACE,{"disambiguationData":[OD(1.0)],"derivedFrom":subQ6})])],"derivedFrom":makeQuery(id+"F3.boolean.opBoolean","SPLIT",EDGE,{"disambiguationData":[TD([subQ6])],"derivedFrom":makeQuery(id+"F1.opRevolve","SWEPT_EDGE",EDGE,{"disambiguationData":[OSD([subQ0,subQ2])]})})})});}
            var Q17;
            Q17=makeQuery(id+"Fq1PH19bnDTYdRj_1.3.F3.boolean.opBoolean","INTERSECT",EDGE,{"disambiguationData":[OD(0.0)],"derivedFrom":[makeQuery(id+"F1.opRevolve","SWEPT_FACE",FACE,{"disambiguationData":[OSD([sQuery(id+"F0.wireOp",EDGE,"E1")])]}),makeQuery(id+"Fq1PH19bnDTYdRj_1.3.F3.opExtrude","SWEPT_FACE",FACE,{"disambiguationData":[OSD([sQuery(id+"F2.wireOp",EDGE,"E16.MirrorCS")])]})]});
            var Q18;
            Q18=makeQuery(id+"F3.boolean.opBoolean","INTERSECT",EDGE,{"disambiguationData":[OD(1.0)],"derivedFrom":[makeQuery(id+"F1.opRevolve","SWEPT_FACE",FACE,{"disambiguationData":[OSD([sQuery(id+"F0.wireOp",EDGE,"E1")])]}),makeQuery(id+"F3.opExtrude","SWEPT_FACE",FACE,{"disambiguationData":[OSD([sQuery(id+"F2.wireOp",EDGE,"E16.MirrorCS")])]})]});
            var Q19;
            Q19=makeQuery(id+"F3.boolean.opBoolean","INTERSECT",EDGE,{"disambiguationData":[OD(1.0)],"derivedFrom":[makeQuery(id+"F1.opRevolve","SWEPT_FACE",FACE,{"disambiguationData":[OSD([sQuery(id+"F0.wireOp",EDGE,"E1")])]}),makeQuery(id+"F3.opExtrude","SWEPT_FACE",FACE,{"disambiguationData":[OSD([sQuery(id+"F2.wireOp",EDGE,"E15")])]})]});
            var Q20;
            {var subQ0=sQuery(id+"F0.wireOp",EDGE,"E1");var subQ2=sQuery(id+"F2.wireOp",EDGE,"E16.MirrorCS");var subQ3=sQuery(id+"F0.wireOp",EDGE,"E13");var subQ5=makeQuery(id+"F3.opExtrude","SWEPT_FACE",FACE,{"disambiguationData":[OSD([subQ2])]});var subQ6=makeQuery(id+"F3.boolean.opBoolean","COPY",FACE,{"disambiguationData":[OD(1.0)],"derivedFrom":subQ5});Q20=makeQuery(id+"Fq1PH19bnDTYdRj_1.3.F3.boolean.opBoolean","SPLIT",EDGE,{"disambiguationData":[TD([subQ6])],"derivedFrom":makeQuery(id+"Fq1PH19bnDTYdRj_1.2.F3.boolean.opBoolean","SPLIT",EDGE,{"disambiguationData":[TD([subQ6])],"derivedFrom":makeQuery(id+"Fq1PH19bnDTYdRj_1.1.F3.boolean.opBoolean","SPLIT",EDGE,{"disambiguationData":[TD([subQ6])],"derivedFrom":makeQuery(id+"F3.boolean.opBoolean","SPLIT",EDGE,{"disambiguationData":[TD([subQ5])],"derivedFrom":makeQuery(id+"F1.opRevolve","SWEPT_EDGE",EDGE,{"disambiguationData":[OSD([subQ0,subQ3])]})})})})});}
            var Q21;
            {var subQ0=sQuery(id+"F0.wireOp",EDGE,"E1");var subQ2=sQuery(id+"F0.wireOp",EDGE,"E13");var subQ4=makeQuery(id+"F3.opExtrude","SWEPT_FACE",FACE,{"disambiguationData":[OSD([sQuery(id+"F2.wireOp",EDGE,"E15")])]});Q21=makeQuery(id+"Fq1PH19bnDTYdRj_1.1.F3.boolean.opBoolean","SPLIT",EDGE,{"disambiguationData":[TD([makeQuery(id+"F3.boolean.opBoolean","COPY",FACE,{"disambiguationData":[OD(1.0)],"derivedFrom":subQ4})])],"derivedFrom":makeQuery(id+"F3.boolean.opBoolean","SPLIT",EDGE,{"disambiguationData":[TD([subQ4])],"derivedFrom":makeQuery(id+"F1.opRevolve","SWEPT_EDGE",EDGE,{"disambiguationData":[OSD([subQ0,subQ2])]})})});}
            var Q22;
            Q22=makeQuery(id+"Fq1PH19bnDTYdRj_1.1.F3.boolean.opBoolean","INTERSECT",EDGE,{"disambiguationData":[OD(1.0)],"derivedFrom":[makeQuery(id+"F1.opRevolve","SWEPT_FACE",FACE,{"disambiguationData":[OSD([sQuery(id+"F0.wireOp",EDGE,"E1")])]}),makeQuery(id+"Fq1PH19bnDTYdRj_1.1.F3.opExtrude","SWEPT_FACE",FACE,{"disambiguationData":[OSD([sQuery(id+"F2.wireOp",EDGE,"E16.MirrorCS")])]})]});
            var Q23;
            Q23=makeQuery(id+"Fq1PH19bnDTYdRj_1.1.F3.boolean.opBoolean","INTERSECT",EDGE,{"disambiguationData":[OD(1.0)],"derivedFrom":[makeQuery(id+"F1.opRevolve","SWEPT_FACE",FACE,{"disambiguationData":[OSD([sQuery(id+"F0.wireOp",EDGE,"E1")])]}),makeQuery(id+"Fq1PH19bnDTYdRj_1.1.F3.opExtrude","SWEPT_FACE",FACE,{"disambiguationData":[OSD([sQuery(id+"F2.wireOp",EDGE,"E15")])]})]});
            fillet(context, id + "F9", {"entities" : qUnion([Q0, Q1, Q2, Q3, Q4, Q5, Q6, Q7, Q8, Q9, Q10, Q11, Q12, Q13, Q14, Q15, Q16, Q17, Q18, Q19, Q20, Q21, Q22, Q23]), "radius" : 1 * mm, "tangentPropagation" : true, "allowEdgeOverflow" : false});
        }
        {
            var Q0;
            Q0=makeQuery(id+"F7.opExtrude","SWEPT_FACE",FACE,{"disambiguationData":[OSD([sQuery(id+"F6.wireOp",EDGE,"E20.left")])]});
            var sketch = newSketch(context, id + "F10", { "sketchPlane" : qUnion([Q0])});
            skCircle(sketch, "E23", {"center": v(-80, 26) * mm, "radius": 3.1 * mm});
            skLineSegment(sketch, "E24", {"start": v(-80, 41) * mm, "end": v(-80, 11) * mm, "construction": true});
            skSolve(sketch);
        }
        {
            var Q0;
            Q0=makeQuery(id+"F10.imprint","IMPRINT",FACE,{"disambiguationData":[TD([[makeQuery(id+"F10.imprint","IMPRINT",EDGE,{"derivedFrom":sQuery(id+"F10.wireOp",EDGE,"E23")}),1.0]])]});
            extrude(context, id + "F11", {"entities" : qUnion([Q0]), "operationType" : NewBodyOperationType.REMOVE, "endBound" : BoundingType.THROUGH_ALL, "oppositeDirection" : true, "depth" : 25 * mm, "offsetDistance" : 25 * mm});
        }
        {
            var Q0;
            Q0=makeQuery(id+"F7.opExtrude","CAP_EDGE",EDGE,{"disambiguationData":[OSD([sQuery(id+"F6.wireOp",EDGE,"E22.3.0.2")])],"isStart":true});
            var Q1;
            Q1=makeQuery(id+"F7.opExtrude","CAP_EDGE",EDGE,{"disambiguationData":[OSD([sQuery(id+"F6.wireOp",EDGE,"E22.2.0.2")])],"isStart":true});
            var Q2;
            Q2=makeQuery(id+"F7.opExtrude","CAP_EDGE",EDGE,{"disambiguationData":[OSD([sQuery(id+"F6.wireOp",EDGE,"E22.1.0.2")])],"isStart":true});
            var Q3;
            Q3=makeQuery(id+"F7.opExtrude","CAP_EDGE",EDGE,{"disambiguationData":[OSD([sQuery(id+"F6.wireOp",EDGE,"E20.bottom")])],"isStart":true});
            var Q4;
            Q4=makeQuery(id+"F7.opExtrude","CAP_EDGE",EDGE,{"disambiguationData":[OSD([sQuery(id+"F6.wireOp",EDGE,"E22.3.0.3")])],"isStart":true});
            var Q5;
            Q5=makeQuery(id+"F7.opExtrude","CAP_EDGE",EDGE,{"disambiguationData":[OSD([sQuery(id+"F6.wireOp",EDGE,"E22.2.0.3")])],"isStart":true});
            var Q6;
            Q6=makeQuery(id+"F7.opExtrude","CAP_EDGE",EDGE,{"disambiguationData":[OSD([sQuery(id+"F6.wireOp",EDGE,"E22.1.0.3")])],"isStart":true});
            var Q7;
            Q7=makeQuery(id+"F7.opExtrude","CAP_EDGE",EDGE,{"disambiguationData":[OSD([sQuery(id+"F6.wireOp",EDGE,"E21")])],"isStart":true});
            var Q8;
            Q8=makeQuery(id+"F7.opExtrude","SWEPT_EDGE",EDGE,{"disambiguationData":[OSD([sQuery(id+"F6.wireOp",EDGE,"E22.3.0.0"),sQuery(id+"F6.wireOp",EDGE,"E22.3.0.2")])]});
            var Q9;
            Q9=makeQuery(id+"F7.opExtrude","CAP_EDGE",EDGE,{"disambiguationData":[OSD([sQuery(id+"F6.wireOp",EDGE,"E22.3.0.0")])],"isStart":true});
            var Q10;
            Q10=makeQuery(id+"F7.opExtrude","SWEPT_EDGE",EDGE,{"disambiguationData":[OSD([sQuery(id+"F6.wireOp",EDGE,"E22.3.0.0"),sQuery(id+"F6.wireOp",EDGE,"E22.3.0.3")])]});
            var Q11;
            Q11=makeQuery(id+"F7.opExtrude","SWEPT_EDGE",EDGE,{"disambiguationData":[OSD([sQuery(id+"F6.wireOp",EDGE,"E20.bottom"),sQuery(id+"F6.wireOp",EDGE,"E20.left")])]});
            var Q12;
            Q12=makeQuery(id+"F7.opExtrude","CAP_EDGE",EDGE,{"disambiguationData":[OSD([sQuery(id+"F6.wireOp",EDGE,"E20.left")])],"isStart":true});
            var Q13;
            Q13=makeQuery(id+"F7.opExtrude","SWEPT_EDGE",EDGE,{"disambiguationData":[OSD([sQuery(id+"F6.wireOp",EDGE,"E20.left"),sQuery(id+"F6.wireOp",EDGE,"E21")])]});
            fillet(context, id + "F12", {"entities" : qUnion([Q0, Q1, Q2, Q3, Q4, Q5, Q6, Q7, Q8, Q9, Q10, Q11, Q12, Q13]), "radius" : 5 * mm, "tangentPropagation" : true, "allowEdgeOverflow" : false});
        }
        {
            var Q0;
            Q0=makeQuery(id+"F1.opRevolve","SWEPT_EDGE",EDGE,{"disambiguationData":[OSD([sQuery(id+"F0.wireOp",EDGE,"E0.right"),sQuery(id+"F0.wireOp",EDGE,"E14")])]});
            fillet(context, id + "F13", {"entities" : qUnion([Q0]), "radius" : 2 * mm, "tangentPropagation" : true, "allowEdgeOverflow" : false});
        }
        {
            var Q0;
            Q0=makeQuery(id+"F1.opRevolve","SWEPT_EDGE",EDGE,{"disambiguationData":[OSD([sQuery(id+"F0.wireOp",EDGE,"E9"),sQuery(id+"F0.wireOp",EDGE,"E10")])]});
            fillet(context, id + "F14", {"entities" : qUnion([Q0]), "radius" : 0.5 * mm, "tangentPropagation" : true, "allowEdgeOverflow" : false});
        }
    });
